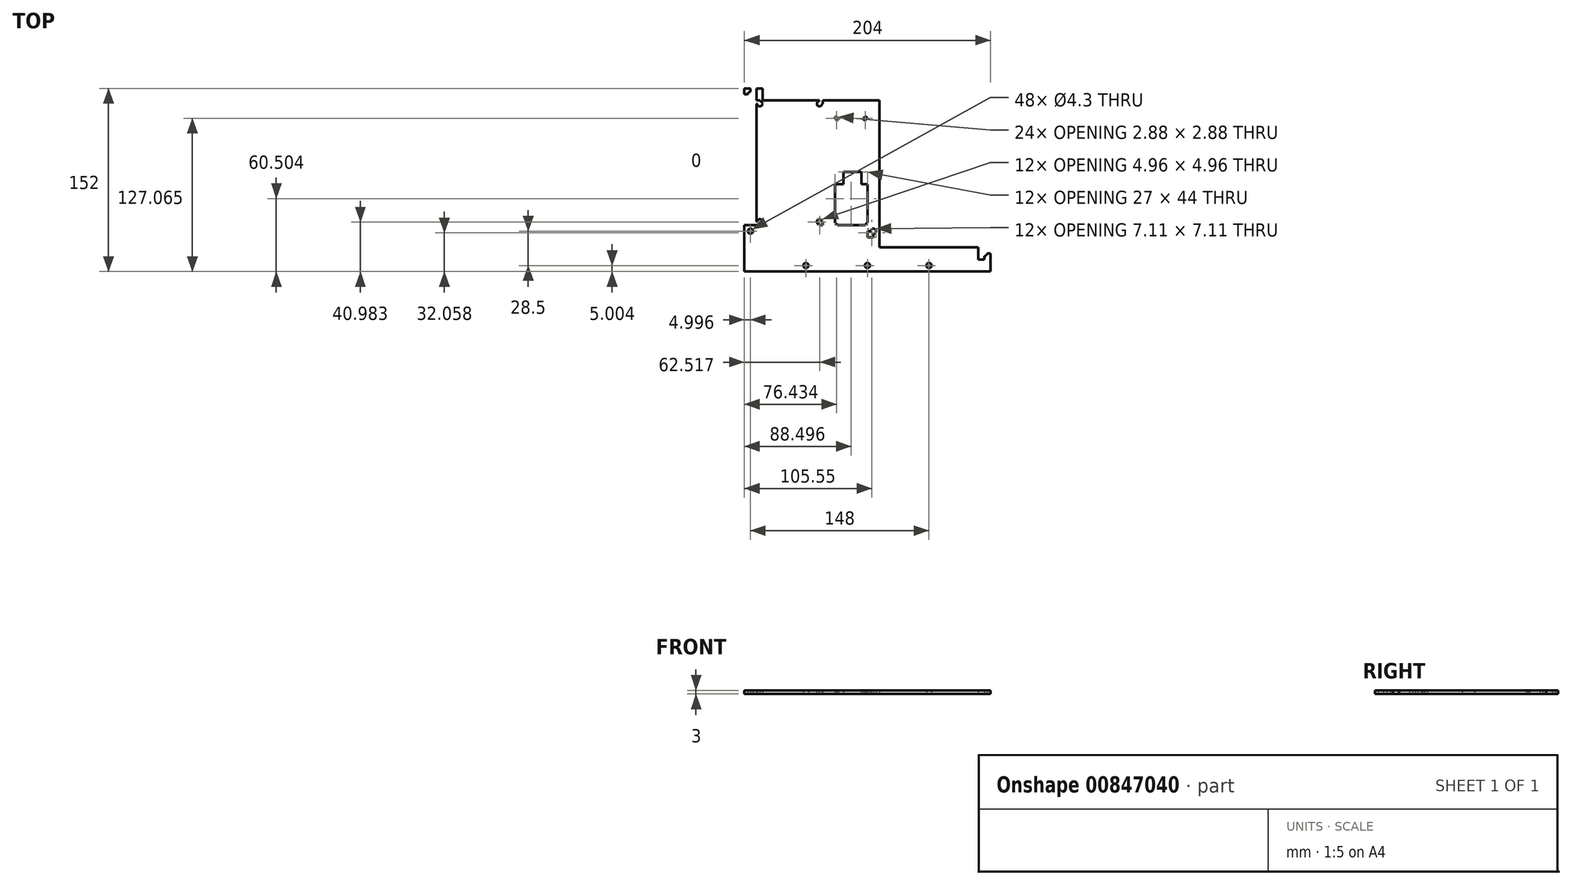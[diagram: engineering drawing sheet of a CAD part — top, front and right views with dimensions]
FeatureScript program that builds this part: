
annotation { "Feature Type Name" : "Feature", "Feature Type Description" : "" }
export const myFeature = defineFeature(function(context is Context, id is Id, definition is map)
    precondition{}
    {
        {
            var Q0;
            Q0=qCreatedBy(makeId("Top.planeOp"),FACE);
            var sketch = newSketch(context, id + "F0", { "sketchPlane" : qUnion([Q0])});
            skLineSegment(sketch, "E0.bottom", {"start": v(-139.34, -2.26) * mm, "end": v(64.66, -2.26) * mm});
            skLineSegment(sketch, "E0.top", {"start": v(-139.34, -144.26) * mm, "end": v(64.66, -144.26) * mm});
            skLineSegment(sketch, "E0.left", {"start": v(-139.34, -2.26) * mm, "end": v(-139.34, -144.26) * mm});
            skLineSegment(sketch, "E0.right", {"start": v(64.66, -2.26) * mm, "end": v(64.66, -144.26) * mm});
            skLineSegment(sketch, "E1.bottom", {"start": v(-139.34, -2.26) * mm, "end": v(-129.34, -2.26) * mm});
            skLineSegment(sketch, "E1.top", {"start": v(-139.34, -12.26) * mm, "end": v(-129.34, -12.26) * mm});
            skLineSegment(sketch, "E1.left", {"start": v(-139.34, -2.26) * mm, "end": v(-139.34, -12.26) * mm});
            skLineSegment(sketch, "E1.right", {"start": v(-129.34, -2.26) * mm, "end": v(-129.34, -12.26) * mm});
            skLineSegment(sketch, "E2.bottom", {"start": v(-129.34, -12.26) * mm, "end": v(-74.34, -12.26) * mm});
            skLineSegment(sketch, "E2.top", {"start": v(-129.34, -115.76) * mm, "end": v(-74.34, -115.76) * mm});
            skLineSegment(sketch, "E2.left", {"start": v(-129.34, -12.26) * mm, "end": v(-129.34, -115.76) * mm});
            skLineSegment(sketch, "E2.right", {"start": v(-74.34, -12.26) * mm, "end": v(-74.34, -115.76) * mm});
            skLineSegment(sketch, "E3", {"start": v(-74.34, -115.76) * mm, "end": v(-64.34, -115.76) * mm});
            skLineSegment(sketch, "E4.bottom", {"start": v(-64.34, -115.76) * mm, "end": v(-37.34, -115.76) * mm});
            skLineSegment(sketch, "E4.top", {"start": v(-64.34, -81.76) * mm, "end": v(-37.34, -81.76) * mm});
            skLineSegment(sketch, "E4.left", {"start": v(-64.34, -115.76) * mm, "end": v(-64.34, -81.76) * mm});
            skLineSegment(sketch, "E4.right", {"start": v(-37.34, -115.76) * mm, "end": v(-37.34, -81.76) * mm});
            skLineSegment(sketch, "E5", {"start": v(-37.34, -81.76) * mm, "end": v(-42.34, -81.76) * mm});
            skLineSegment(sketch, "E6.bottom", {"start": v(-42.34, -81.76) * mm, "end": v(-57.34, -81.76) * mm});
            skLineSegment(sketch, "E6.top", {"start": v(-42.34, -71.76) * mm, "end": v(-57.34, -71.76) * mm});
            skLineSegment(sketch, "E6.left", {"start": v(-42.34, -81.76) * mm, "end": v(-42.34, -71.76) * mm});
            skLineSegment(sketch, "E6.right", {"start": v(-57.34, -81.76) * mm, "end": v(-57.34, -71.76) * mm});
            skLineSegment(sketch, "E7", {"start": v(-64.34, -81.76) * mm, "end": v(-64.34, -61.76) * mm});
            skLineSegment(sketch, "E8.bottom", {"start": v(-64.34, -61.76) * mm, "end": v(-37.84, -61.76) * mm});
            skLineSegment(sketch, "E8.top", {"start": v(-64.34, -25.76) * mm, "end": v(-37.84, -25.76) * mm});
            skLineSegment(sketch, "E8.left", {"start": v(-64.34, -61.76) * mm, "end": v(-64.34, -25.76) * mm});
            skLineSegment(sketch, "E8.right", {"start": v(-37.84, -61.76) * mm, "end": v(-37.84, -25.76) * mm});
            skLineSegment(sketch, "E9", {"start": v(-74.34, -12.26) * mm, "end": v(-27.34, -12.26) * mm});
            skLineSegment(sketch, "E10", {"start": v(-27.34, -12.26) * mm, "end": v(-27.34, -134.26) * mm});
            skLineSegment(sketch, "E11", {"start": v(-27.34, -134.26) * mm, "end": v(54.66, -134.26) * mm});
            skLineSegment(sketch, "E12.bottom", {"start": v(54.66, -134.26) * mm, "end": v(-27.34, -134.26) * mm});
            skLineSegment(sketch, "E12.top", {"start": v(54.66, -12.26) * mm, "end": v(-27.34, -12.26) * mm});
            skLineSegment(sketch, "E12.left", {"start": v(54.66, -134.26) * mm, "end": v(54.66, -12.26) * mm});
            skLineSegment(sketch, "E12.right", {"start": v(-27.34, -134.26) * mm, "end": v(-27.34, -12.26) * mm});
            skLineSegment(sketch, "E13.bottom", {"start": v(-129.34, -115.76) * mm, "end": v(-139.34, -115.76) * mm});
            skLineSegment(sketch, "E13.top", {"start": v(-129.34, -125.76) * mm, "end": v(-139.34, -125.76) * mm});
            skLineSegment(sketch, "E13.left", {"start": v(-129.34, -115.76) * mm, "end": v(-129.34, -125.76) * mm});
            skLineSegment(sketch, "E13.right", {"start": v(-139.34, -115.76) * mm, "end": v(-139.34, -125.76) * mm});
            skLineSegment(sketch, "E14.bottom", {"start": v(-37.34, -115.76) * mm, "end": v(-27.34, -115.76) * mm});
            skLineSegment(sketch, "E14.top", {"start": v(-37.34, -125.76) * mm, "end": v(-27.34, -125.76) * mm});
            skLineSegment(sketch, "E14.left", {"start": v(-37.34, -115.76) * mm, "end": v(-37.34, -125.76) * mm});
            skLineSegment(sketch, "E14.right", {"start": v(-27.34, -115.76) * mm, "end": v(-27.34, -125.76) * mm});
            skLineSegment(sketch, "E15.top", {"start": v(-139.34, -125.76) * mm, "end": v(-37.34, -125.76) * mm});
            skLineSegment(sketch, "E15.left", {"start": v(-139.34, -144.26) * mm, "end": v(-139.34, -125.76) * mm});
            skLineSegment(sketch, "E15.right", {"start": v(-37.34, -144.26) * mm, "end": v(-37.34, -125.76) * mm});
            skLineSegment(sketch, "E16", {"start": v(-129.34, -12.26) * mm, "end": v(-124.4, -12.26) * mm});
            skLineSegment(sketch, "E17", {"start": v(-124.4, -12.26) * mm, "end": v(-124.4, -2.26) * mm});
            skLineSegment(sketch, "E18", {"start": v(-74.34, -12.26) * mm, "end": v(-79.34, -12.26) * mm});
            skLineSegment(sketch, "E19", {"start": v(-79.34, -12.26) * mm, "end": v(-79.34, -2.26) * mm});
            skLineSegment(sketch, "E20.bottom", {"start": v(-129.34, -12.26) * mm, "end": v(-126.54, -12.26) * mm});
            skLineSegment(sketch, "E20.top", {"start": v(-129.34, -15.06) * mm, "end": v(-126.54, -15.06) * mm});
            skLineSegment(sketch, "E20.left", {"start": v(-129.34, -12.26) * mm, "end": v(-129.34, -15.06) * mm});
            skLineSegment(sketch, "E20.right", {"start": v(-126.54, -12.26) * mm, "end": v(-126.54, -15.06) * mm});
            skLineSegment(sketch, "E21.bottom", {"start": v(-129.34, -115.76) * mm, "end": v(-126.54, -115.76) * mm});
            skLineSegment(sketch, "E21.top", {"start": v(-129.34, -112.96) * mm, "end": v(-126.54, -112.96) * mm});
            skLineSegment(sketch, "E21.left", {"start": v(-129.34, -115.76) * mm, "end": v(-129.34, -112.96) * mm});
            skLineSegment(sketch, "E21.right", {"start": v(-126.54, -115.76) * mm, "end": v(-126.54, -112.96) * mm});
            skLineSegment(sketch, "E22.bottom", {"start": v(-74.34, -115.76) * mm, "end": v(-77.2, -115.76) * mm});
            skLineSegment(sketch, "E22.top", {"start": v(-74.34, -112.9) * mm, "end": v(-77.2, -112.9) * mm});
            skLineSegment(sketch, "E22.left", {"start": v(-74.34, -115.76) * mm, "end": v(-74.34, -112.9) * mm});
            skLineSegment(sketch, "E22.right", {"start": v(-77.2, -115.76) * mm, "end": v(-77.2, -112.9) * mm});
            skLineSegment(sketch, "E23.bottom", {"start": v(-74.34, -12.26) * mm, "end": v(-77.14, -12.26) * mm});
            skLineSegment(sketch, "E23.top", {"start": v(-74.34, -15.06) * mm, "end": v(-77.14, -15.06) * mm});
            skLineSegment(sketch, "E23.left", {"start": v(-74.34, -12.26) * mm, "end": v(-74.34, -15.06) * mm});
            skLineSegment(sketch, "E23.right", {"start": v(-77.14, -12.26) * mm, "end": v(-77.14, -15.06) * mm});
            skLineSegment(sketch, "E24.bottom", {"start": v(-27.34, -134.26) * mm, "end": v(-25.14, -134.26) * mm});
            skLineSegment(sketch, "E24.top", {"start": v(-27.34, -132.06) * mm, "end": v(-25.14, -132.06) * mm});
            skLineSegment(sketch, "E24.left", {"start": v(-27.34, -134.26) * mm, "end": v(-27.34, -132.06) * mm});
            skLineSegment(sketch, "E24.right", {"start": v(-25.14, -134.26) * mm, "end": v(-25.14, -132.06) * mm});
            skLineSegment(sketch, "E25.bottom", {"start": v(54.66, -134.26) * mm, "end": v(52.46, -134.26) * mm});
            skLineSegment(sketch, "E25.top", {"start": v(54.66, -132.06) * mm, "end": v(52.46, -132.06) * mm});
            skLineSegment(sketch, "E25.left", {"start": v(54.66, -134.26) * mm, "end": v(54.66, -132.06) * mm});
            skLineSegment(sketch, "E25.right", {"start": v(52.46, -134.26) * mm, "end": v(52.46, -132.06) * mm});
            skLineSegment(sketch, "E26.bottom", {"start": v(54.66, -12.26) * mm, "end": v(52.46, -12.26) * mm});
            skLineSegment(sketch, "E26.top", {"start": v(54.66, -14.46) * mm, "end": v(52.46, -14.46) * mm});
            skLineSegment(sketch, "E26.left", {"start": v(54.66, -12.26) * mm, "end": v(54.66, -14.46) * mm});
            skLineSegment(sketch, "E26.right", {"start": v(52.46, -12.26) * mm, "end": v(52.46, -14.46) * mm});
            skLineSegment(sketch, "E27.bottom", {"start": v(-27.34, -12.26) * mm, "end": v(-25.14, -12.26) * mm});
            skLineSegment(sketch, "E27.top", {"start": v(-27.34, -14.46) * mm, "end": v(-25.14, -14.46) * mm});
            skLineSegment(sketch, "E27.left", {"start": v(-27.34, -12.26) * mm, "end": v(-27.34, -14.46) * mm});
            skLineSegment(sketch, "E27.right", {"start": v(-25.14, -12.26) * mm, "end": v(-25.14, -14.46) * mm});
            skLineSegment(sketch, "E28.bottom", {"start": v(-37.84, -61.76) * mm, "end": v(-39.6, -61.76) * mm});
            skLineSegment(sketch, "E28.left", {"start": v(-37.84, -61.76) * mm, "end": v(-37.84, -60) * mm});
            skLineSegment(sketch, "E29.bottom", {"start": v(-37.84, -25.76) * mm, "end": v(-39.54, -25.76) * mm});
            skLineSegment(sketch, "E29.top", {"start": v(-37.84, -27.46) * mm, "end": v(-39.54, -27.46) * mm});
            skLineSegment(sketch, "E29.left", {"start": v(-37.84, -25.76) * mm, "end": v(-37.84, -27.46) * mm});
            skLineSegment(sketch, "E29.right", {"start": v(-39.54, -25.76) * mm, "end": v(-39.54, -27.46) * mm});
            skLineSegment(sketch, "E30.bottom", {"start": v(-64.34, -25.76) * mm, "end": v(-62.64, -25.76) * mm});
            skLineSegment(sketch, "E30.top", {"start": v(-64.34, -27.46) * mm, "end": v(-62.64, -27.46) * mm});
            skLineSegment(sketch, "E30.left", {"start": v(-64.34, -25.76) * mm, "end": v(-64.34, -27.46) * mm});
            skLineSegment(sketch, "E30.right", {"start": v(-62.64, -25.76) * mm, "end": v(-62.64, -27.46) * mm});
            skLineSegment(sketch, "E31.bottom", {"start": v(-64.34, -61.76) * mm, "end": v(-62.6, -61.76) * mm});
            skLineSegment(sketch, "E31.left", {"start": v(-64.34, -61.76) * mm, "end": v(-64.34, -60) * mm});
            skLineSegment(sketch, "E32.bottom", {"start": v(-64.34, -115.76) * mm, "end": v(-62.4, -115.76) * mm});
            skLineSegment(sketch, "E32.top", {"start": v(-64.34, -113.8) * mm, "end": v(-62.4, -113.8) * mm});
            skLineSegment(sketch, "E32.left", {"start": v(-64.34, -115.76) * mm, "end": v(-64.34, -113.8) * mm});
            skLineSegment(sketch, "E32.right", {"start": v(-62.4, -115.76) * mm, "end": v(-62.4, -113.8) * mm});
            skLineSegment(sketch, "E33.bottom", {"start": v(-37.34, -115.76) * mm, "end": v(-39.3, -115.76) * mm});
            skLineSegment(sketch, "E33.top", {"start": v(-37.34, -113.8) * mm, "end": v(-39.3, -113.8) * mm});
            skLineSegment(sketch, "E33.left", {"start": v(-37.34, -115.76) * mm, "end": v(-37.34, -113.8) * mm});
            skLineSegment(sketch, "E33.right", {"start": v(-39.3, -115.76) * mm, "end": v(-39.3, -113.8) * mm});
            skLineSegment(sketch, "E34.bottom", {"start": v(-37.34, -81.76) * mm, "end": v(-39.3, -81.76) * mm});
            skLineSegment(sketch, "E34.top", {"start": v(-37.34, -83.7) * mm, "end": v(-39.3, -83.7) * mm});
            skLineSegment(sketch, "E34.left", {"start": v(-37.34, -81.76) * mm, "end": v(-37.34, -83.7) * mm});
            skLineSegment(sketch, "E34.right", {"start": v(-39.3, -81.76) * mm, "end": v(-39.3, -83.7) * mm});
            skLineSegment(sketch, "E35.bottom", {"start": v(-64.34, -81.76) * mm, "end": v(-62.4, -81.76) * mm});
            skLineSegment(sketch, "E35.top", {"start": v(-64.34, -83.7) * mm, "end": v(-62.4, -83.7) * mm});
            skLineSegment(sketch, "E35.left", {"start": v(-64.34, -81.76) * mm, "end": v(-64.34, -83.7) * mm});
            skLineSegment(sketch, "E35.right", {"start": v(-62.4, -81.76) * mm, "end": v(-62.4, -83.7) * mm});
            skCircle(sketch, "E36", {"center": v(-126.54, -15.06) * mm, "radius": 2.15 * mm});
            skCircle(sketch, "E37", {"center": v(-77.14, -15.06) * mm, "radius": 2.15 * mm});
            skCircle(sketch, "E38", {"center": v(-126.54, -112.96) * mm, "radius": 2.15 * mm});
            skCircle(sketch, "E39", {"center": v(-77.2, -112.9) * mm, "radius": 2.15 * mm});
            skCircle(sketch, "E40", {"center": v(-25.14, -132.06) * mm, "radius": 1.4 * mm});
            skCircle(sketch, "E41", {"center": v(52.46, -132.06) * mm, "radius": 1.4 * mm});
            skCircle(sketch, "E42", {"center": v(-25.14, -14.46) * mm, "radius": 1.4 * mm});
            skCircle(sketch, "E43", {"center": v(52.46, -14.46) * mm, "radius": 1.4 * mm});
            skCircle(sketch, "E44", {"center": v(-39.3, -113.8) * mm, "radius": 1.15 * mm});
            skCircle(sketch, "E45", {"center": v(-62.4, -113.8) * mm, "radius": 1.15 * mm});
            skCircle(sketch, "E46", {"center": v(-62.4, -83.7) * mm, "radius": 1.15 * mm});
            skCircle(sketch, "E47", {"center": v(-39.3, -83.7) * mm, "radius": 1.15 * mm});
            skCircle(sketch, "E48", {"center": v(-62.64, -27.46) * mm, "radius": 1.2 * mm});
            skCircle(sketch, "E49", {"center": v(-39.54, -27.46) * mm, "radius": 1.2 * mm});
            skLineSegment(sketch, "E50.bottom", {"start": v(-37.34, -144.26) * mm, "end": v(-139.34, -144.26) * mm});
            skLineSegment(sketch, "E50.top", {"start": v(-37.34, -125.76) * mm, "end": v(-139.34, -125.76) * mm});
            skLineSegment(sketch, "E51.bottom", {"start": v(54.66, -134.26) * mm, "end": v(34.66, -134.26) * mm});
            skLineSegment(sketch, "E51.top", {"start": v(54.66, -144.26) * mm, "end": v(34.66, -144.26) * mm});
            skLineSegment(sketch, "E51.left", {"start": v(54.66, -134.26) * mm, "end": v(54.66, -144.26) * mm});
            skLineSegment(sketch, "E51.right", {"start": v(34.66, -134.26) * mm, "end": v(34.66, -144.26) * mm});
            skLineSegment(sketch, "E52.top", {"start": v(-139.34, -154.26) * mm, "end": v(64.66, -154.26) * mm});
            skLineSegment(sketch, "E52.left", {"start": v(-139.34, -144.26) * mm, "end": v(-139.34, -154.26) * mm});
            skLineSegment(sketch, "E52.right", {"start": v(64.66, -144.26) * mm, "end": v(64.66, -154.26) * mm});
            skLineSegment(sketch, "E53", {"start": v(-139.34, -144.26) * mm, "end": v(-88.34, -144.26) * mm});
            skLineSegment(sketch, "E54", {"start": v(-88.34, -144.26) * mm, "end": v(-37.34, -144.26) * mm});
            skLineSegment(sketch, "E55", {"start": v(-37.34, -144.26) * mm, "end": v(13.66, -144.26) * mm});
            skPoint(sketch, "E55.endSnap0", {"position": v(13.66, -134.26) * mm});
            skLineSegment(sketch, "E56.left", {"start": v(-139.34, -144.26) * mm, "end": v(-139.34, -149.26) * mm});
            skLineSegment(sketch, "E56.right", {"start": v(-88.34, -144.26) * mm, "end": v(-88.34, -149.26) * mm});
            skLineSegment(sketch, "E57.bottom", {"start": v(-37.34, -144.26) * mm, "end": v(-88.34, -144.26) * mm});
            skLineSegment(sketch, "E57.left", {"start": v(-37.34, -144.26) * mm, "end": v(-37.34, -149.26) * mm});
            skLineSegment(sketch, "E58.bottom", {"start": v(13.66, -144.26) * mm, "end": v(-37.34, -144.26) * mm});
            skCircle(sketch, "E59", {"center": v(-88.34, -149.26) * mm, "radius": 2.15 * mm});
            skCircle(sketch, "E60", {"center": v(-37.34, -149.26) * mm, "radius": 2.15 * mm});
            skCircle(sketch, "E61", {"center": v(13.66, -149.26) * mm, "radius": 2.15 * mm});
            skLineSegment(sketch, "E62", {"start": v(-27.34, -134.26) * mm, "end": v(-27.34, -144.26) * mm});
            skLineSegment(sketch, "E63.bottom", {"start": v(-139.34, -125.76) * mm, "end": v(-134.34, -125.76) * mm});
            skLineSegment(sketch, "E63.top", {"start": v(-139.34, -120.76) * mm, "end": v(-134.34, -120.76) * mm});
            skLineSegment(sketch, "E63.left", {"start": v(-139.34, -125.76) * mm, "end": v(-139.34, -120.76) * mm});
            skLineSegment(sketch, "E63.right", {"start": v(-134.34, -125.76) * mm, "end": v(-134.34, -120.76) * mm});
            skLineSegment(sketch, "E64.bottom", {"start": v(-139.34, -2.26) * mm, "end": v(-134.34, -2.26) * mm});
            skLineSegment(sketch, "E64.top", {"start": v(-139.34, -7.26) * mm, "end": v(-134.34, -7.26) * mm});
            skLineSegment(sketch, "E64.left", {"start": v(-139.34, -2.26) * mm, "end": v(-139.34, -7.26) * mm});
            skLineSegment(sketch, "E64.right", {"start": v(-134.34, -2.26) * mm, "end": v(-134.34, -7.26) * mm});
            skLineSegment(sketch, "E65.bottom", {"start": v(-37.34, -125.76) * mm, "end": v(-32.34, -125.76) * mm});
            skLineSegment(sketch, "E65.top", {"start": v(-37.34, -120.76) * mm, "end": v(-32.34, -120.76) * mm});
            skLineSegment(sketch, "E65.left", {"start": v(-37.34, -125.76) * mm, "end": v(-37.34, -120.76) * mm});
            skLineSegment(sketch, "E65.right", {"start": v(-32.34, -125.76) * mm, "end": v(-32.34, -120.76) * mm});
            skLineSegment(sketch, "E66.bottom", {"start": v(64.66, -144.26) * mm, "end": v(59.66, -144.26) * mm});
            skLineSegment(sketch, "E66.top", {"start": v(64.66, -139.26) * mm, "end": v(59.66, -139.26) * mm});
            skLineSegment(sketch, "E66.left", {"start": v(64.66, -144.26) * mm, "end": v(64.66, -139.26) * mm});
            skLineSegment(sketch, "E66.right", {"start": v(59.66, -144.26) * mm, "end": v(59.66, -139.26) * mm});
            skCircle(sketch, "E67", {"center": v(59.66, -139.26) * mm, "radius": 2.15 * mm});
            skCircle(sketch, "E68", {"center": v(-134.34, -120.76) * mm, "radius": 2.15 * mm});
            skCircle(sketch, "E69", {"center": v(-32.34, -120.76) * mm, "radius": 2.15 * mm});
            skCircle(sketch, "E70", {"center": v(-134.34, -7.26) * mm, "radius": 2.15 * mm});
            skSolve(sketch);
        }
        {
            var Q0;
            Q0=makeQuery(id+"F0.imprint","IMPRINT",FACE,{"disambiguationData":[TD([[makeQuery(id+"F0.imprint","IMPRINT",EDGE,{"derivedFrom":sQuery(id+"F0.wireOp",EDGE,"E2.right")}),1.0]])]});
            var Q1;
            Q1=makeQuery(id+"F0.imprint","IMPRINT",FACE,{"disambiguationData":[TD([[makeQuery(id+"F0.imprint","IMPRINT",EDGE,{"derivedFrom":sQuery(id+"F0.wireOp",EDGE,"E14.bottom")}),-1.0]])]});
            var Q2;
            Q2=makeQuery(id+"F0.imprint","IMPRINT",FACE,{"disambiguationData":[TD([[makeQuery(id+"F0.imprint","IMPRINT",EDGE,{"derivedFrom":sQuery(id+"F0.wireOp",EDGE,"E2.top")}),-1.0]])]});
            var Q3;
            Q3=makeQuery(id+"F0.imprint","IMPRINT",FACE,{"disambiguationData":[TD([[makeQuery(id+"F0.imprint","IMPRINT",EDGE,{"derivedFrom":sQuery(id+"F0.wireOp",EDGE,"E13.bottom")}),1.0]])]});
            var Q4;
            Q4=makeQuery(id+"F0.imprint","IMPRINT",FACE,{"disambiguationData":[TD([[makeQuery(id+"F0.imprint","IMPRINT",EDGE,{"derivedFrom":sQuery(id+"F0.wireOp",EDGE,"E0.left")}),1.0]])]});
            var Q5;
            Q5=makeQuery(id+"F0.imprint","IMPRINT",FACE,{"disambiguationData":[TD([[makeQuery(id+"F0.imprint","IMPRINT",EDGE,{"derivedFrom":sQuery(id+"F0.wireOp",EDGE,"E1.bottom")}),-1.0]])]});
            var Q6;
            {var subQ0=sQuery(id+"F0.wireOp",EDGE,"E1.right");Q6=makeQuery(id+"F0.imprint","IMPRINT",FACE,{"disambiguationData":[TD([[makeQuery(id+"F0.imprint","IMPRINT",EDGE,{"derivedFrom":subQ0}),1.0]])]});}
            var Q7;
            Q7=makeQuery(id+"F0.imprint","IMPRINT",FACE,{"disambiguationData":[TD([[makeQuery(id+"F0.imprint","IMPRINT",EDGE,{"derivedFrom":sQuery(id+"F0.wireOp",EDGE,"E0.top")}),1.0]])]});
            var Q8;
            {var subQ2=sQuery(id+"F0.wireOp",EDGE,"E0.right");Q8=makeQuery(id+"F0.imprint","IMPRINT",FACE,{"disambiguationData":[TD([[makeQuery(id+"F0.imprint","IMPRINT",EDGE,{"derivedFrom":subQ2}),-1.0]])]});}
            var Q9;
            Q9=makeQuery(id+"F0.imprint","IMPRINT",FACE,{"disambiguationData":[TD([[makeQuery(id+"F0.imprint","IMPRINT",EDGE,{"derivedFrom":sQuery(id+"F0.wireOp",EDGE,"E50.bottom")}),-1.0]])]});
            var Q10;
            Q10=makeQuery(id+"F0.imprint","IMPRINT",FACE,{"disambiguationData":[TD([[makeQuery(id+"F0.imprint","IMPRINT",EDGE,{"derivedFrom":sQuery(id+"F0.wireOp",EDGE,"E2.bottom")}),-1.0]])]});
            var Q11;
            Q11=makeQuery(id+"F0.imprint","IMPRINT",FACE,{"disambiguationData":[TD([[makeQuery(id+"F0.imprint","IMPRINT",EDGE,{"derivedFrom":sQuery(id+"F0.wireOp",EDGE,"E2.bottom")}),1.0]])]});
            var Q12;
            {var subQ1=sQuery(id+"F0.wireOp",EDGE,"E4.bottom");Q12=makeQuery(id+"F0.imprint","IMPRINT",FACE,{"disambiguationData":[TD([[makeQuery(id+"F0.imprint","IMPRINT",EDGE,{"derivedFrom":subQ1}),1.0]])]});}
            var Q13;
            Q13=makeQuery(id+"F0.imprint","IMPRINT",FACE,{"disambiguationData":[TD([[makeQuery(id+"F0.imprint","IMPRINT",EDGE,{"derivedFrom":sQuery(id+"F0.wireOp",EDGE,"E8.bottom")}),1.0]])]});
            var Q14;
            {var subQ19=sQuery(id+"F0.wireOp",EDGE,"E12.bottom");Q14=makeQuery(id+"F0.imprint","IMPRINT",FACE,{"disambiguationData":[TD([[makeQuery(id+"F0.imprint","IMPRINT",EDGE,{"derivedFrom":subQ19}),-1.0]])]});}
            var Q15;
            Q15=makeQuery(id+"F0.imprint","IMPRINT",FACE,{"disambiguationData":[TD([[makeQuery(id+"F0.imprint","IMPRINT",EDGE,{"derivedFrom":sQuery(id+"F0.wireOp",EDGE,"E51.top")}),-1.0]])]});
            var Q16;
            {var subQ1=sQuery(id+"F0.wireOp",EDGE,"E21.bottom");Q16=makeQuery(id+"F0.imprint","IMPRINT",FACE,{"disambiguationData":[TD([[makeQuery(id+"F0.imprint","IMPRINT",EDGE,{"derivedFrom":subQ1}),1.0]])]});}
            var Q17;
            {var subQ1=sQuery(id+"F0.wireOp",EDGE,"E32.bottom");Q17=makeQuery(id+"F0.imprint","IMPRINT",FACE,{"disambiguationData":[TD([[makeQuery(id+"F0.imprint","IMPRINT",EDGE,{"derivedFrom":subQ1}),1.0]])]});}
            var Q18;
            {var subQ1=sQuery(id+"F0.wireOp",EDGE,"E22.bottom");Q18=makeQuery(id+"F0.imprint","IMPRINT",FACE,{"disambiguationData":[TD([[makeQuery(id+"F0.imprint","IMPRINT",EDGE,{"derivedFrom":subQ1}),-1.0]])]});}
            var Q19;
            Q19=makeQuery(id+"F0.imprint","IMPRINT",FACE,{"disambiguationData":[TD([[makeQuery(id+"F0.imprint","IMPRINT",EDGE,{"derivedFrom":sQuery(id+"F0.wireOp",EDGE,"E6.bottom")}),-1.0]])]});
            var Q20;
            {var subQ1=sQuery(id+"F0.wireOp",EDGE,"E35.bottom");Q20=makeQuery(id+"F0.imprint","IMPRINT",FACE,{"disambiguationData":[TD([[makeQuery(id+"F0.imprint","IMPRINT",EDGE,{"derivedFrom":subQ1}),-1.0]])]});}
            var Q21;
            {var subQ1=sQuery(id+"F0.wireOp",EDGE,"E34.bottom");Q21=makeQuery(id+"F0.imprint","IMPRINT",FACE,{"disambiguationData":[TD([[makeQuery(id+"F0.imprint","IMPRINT",EDGE,{"derivedFrom":subQ1}),1.0]])]});}
            var Q22;
            {var subQ1=sQuery(id+"F0.wireOp",EDGE,"E33.bottom");Q22=makeQuery(id+"F0.imprint","IMPRINT",FACE,{"disambiguationData":[TD([[makeQuery(id+"F0.imprint","IMPRINT",EDGE,{"derivedFrom":subQ1}),-1.0]])]});}
            var Q23;
            {var subQ1=sQuery(id+"F0.wireOp",EDGE,"E23.bottom");Q23=makeQuery(id+"F0.imprint","IMPRINT",FACE,{"disambiguationData":[TD([[makeQuery(id+"F0.imprint","IMPRINT",EDGE,{"derivedFrom":subQ1}),1.0]])]});}
            var Q24;
            {var subQ1=sQuery(id+"F0.wireOp",EDGE,"E20.bottom");Q24=makeQuery(id+"F0.imprint","IMPRINT",FACE,{"disambiguationData":[TD([[makeQuery(id+"F0.imprint","IMPRINT",EDGE,{"derivedFrom":subQ1}),-1.0]])]});}
            var Q25;
            {var subQ1=sQuery(id+"F0.wireOp",EDGE,"E30.bottom");Q25=makeQuery(id+"F0.imprint","IMPRINT",FACE,{"disambiguationData":[TD([[makeQuery(id+"F0.imprint","IMPRINT",EDGE,{"derivedFrom":subQ1}),-1.0]])]});}
            var Q26;
            {var subQ1=sQuery(id+"F0.wireOp",EDGE,"E29.bottom");Q26=makeQuery(id+"F0.imprint","IMPRINT",FACE,{"disambiguationData":[TD([[makeQuery(id+"F0.imprint","IMPRINT",EDGE,{"derivedFrom":subQ1}),1.0]])]});}
            var Q27;
            {var subQ1=sQuery(id+"F0.wireOp",EDGE,"E26.bottom");Q27=makeQuery(id+"F0.imprint","IMPRINT",FACE,{"disambiguationData":[TD([[makeQuery(id+"F0.imprint","IMPRINT",EDGE,{"derivedFrom":subQ1}),1.0]])]});}
            var Q28;
            {var subQ1=sQuery(id+"F0.wireOp",EDGE,"E27.bottom");Q28=makeQuery(id+"F0.imprint","IMPRINT",FACE,{"disambiguationData":[TD([[makeQuery(id+"F0.imprint","IMPRINT",EDGE,{"derivedFrom":subQ1}),-1.0]])]});}
            var Q29;
            {var subQ1=sQuery(id+"F0.wireOp",EDGE,"E24.bottom");Q29=makeQuery(id+"F0.imprint","IMPRINT",FACE,{"disambiguationData":[TD([[makeQuery(id+"F0.imprint","IMPRINT",EDGE,{"derivedFrom":subQ1}),1.0]])]});}
            var Q30;
            {var subQ5=sQuery(id+"F0.wireOp",EDGE,"E25.left");Q30=makeQuery(id+"F0.imprint","IMPRINT",FACE,{"disambiguationData":[TD([[makeQuery(id+"F0.imprint","IMPRINT",EDGE,{"derivedFrom":subQ5}),1.0]])]});}
            var Q31;
            {var subQ1=sQuery(id+"F0.wireOp",EDGE,"E15.right");Q31=makeQuery(id+"F0.imprint","IMPRINT",FACE,{"disambiguationData":[TD([[makeQuery(id+"F0.imprint","IMPRINT",EDGE,{"derivedFrom":subQ1}),1.0]])]});}
            var Q32;
            {var subQ1=sQuery(id+"F0.wireOp",EDGE,"E51.left");Q32=makeQuery(id+"F0.imprint","IMPRINT",FACE,{"disambiguationData":[TD([[makeQuery(id+"F0.imprint","IMPRINT",EDGE,{"derivedFrom":subQ1}),-1.0]])]});}
            var Q33;
            Q33=makeQuery(id+"F0.imprint","IMPRINT",FACE,{"disambiguationData":[TD([[makeQuery(id+"F0.imprint","IMPRINT",EDGE,{"derivedFrom":sQuery(id+"F0.wireOp",EDGE,"E52.top")}),1.0]])]});
            var Q34;
            {var subQ0=sQuery(id+"F0.wireOp",EDGE,"E14.top");Q34=makeQuery(id+"F0.imprint","IMPRINT",FACE,{"disambiguationData":[TD([[makeQuery(id+"F0.imprint","IMPRINT",EDGE,{"derivedFrom":subQ0}),-1.0]])]});}
            var Q35;
            Q35=makeQuery(id+"F0.imprint","IMPRINT",FACE,{"disambiguationData":[TD([[makeQuery(id+"F0.imprint","IMPRINT",EDGE,{"derivedFrom":sQuery(id+"F0.wireOp",EDGE,"E12.bottom")}),1.0]])]});
            var Q36;
            {var subQ1=sQuery(id+"F0.wireOp",EDGE,"E63.bottom");Q36=makeQuery(id+"F0.imprint","IMPRINT",FACE,{"disambiguationData":[TD([[makeQuery(id+"F0.imprint","IMPRINT",EDGE,{"derivedFrom":subQ1}),1.0]])]});}
            var Q37;
            {var subQ1=sQuery(id+"F0.wireOp",EDGE,"E65.bottom");Q37=makeQuery(id+"F0.imprint","IMPRINT",FACE,{"disambiguationData":[TD([[makeQuery(id+"F0.imprint","IMPRINT",EDGE,{"derivedFrom":subQ1}),1.0]])]});}
            var Q38;
            {var subQ1=sQuery(id+"F0.wireOp",EDGE,"E66.bottom");Q38=makeQuery(id+"F0.imprint","IMPRINT",FACE,{"disambiguationData":[TD([[makeQuery(id+"F0.imprint","IMPRINT",EDGE,{"derivedFrom":subQ1}),-1.0]])]});}
            var Q39;
            {var subQ1=sQuery(id+"F0.wireOp",EDGE,"E64.bottom");Q39=makeQuery(id+"F0.imprint","IMPRINT",FACE,{"disambiguationData":[TD([[makeQuery(id+"F0.imprint","IMPRINT",EDGE,{"derivedFrom":subQ1}),-1.0]])]});}
            extrude(context, id + "F1", {"entities" : qUnion([Q0, Q1, Q2, Q3, Q4, Q5, Q6, Q7, Q8, Q9, Q10, Q11, Q12, Q13, Q14, Q15, Q16, Q17, Q18, Q19, Q20, Q21, Q22, Q23, Q24, Q25, Q26, Q27, Q28, Q29, Q30, Q31, Q32, Q33, Q34, Q35, Q36, Q37, Q38, Q39]), "depth" : 3 * mm, "offsetDistance" : 25 * mm});
        }
    });
